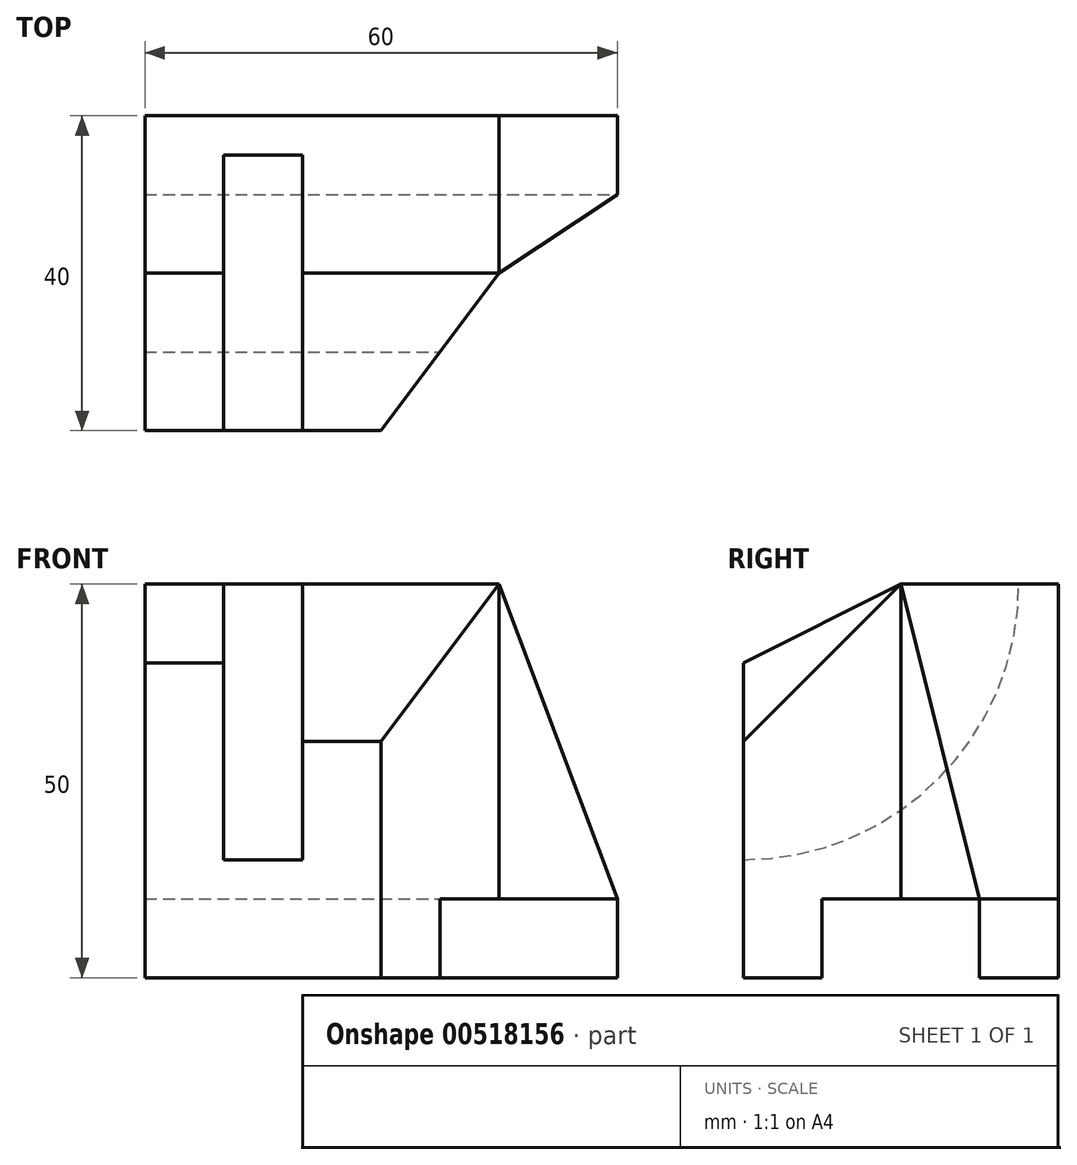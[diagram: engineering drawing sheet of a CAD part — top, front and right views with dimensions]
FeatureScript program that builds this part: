
annotation { "Feature Type Name" : "Feature", "Feature Type Description" : "" }
export const myFeature = defineFeature(function(context is Context, id is Id, definition is map)
    precondition{}
    {
        {
            var Q0;
            Q0=qCreatedBy(makeId("Front.planeOp"),FACE);
            var sketch = newSketch(context, id + "F0", { "sketchPlane" : qUnion([Q0])});
            skLineSegment(sketch, "E0.bottom", {"start": v(0, 0) * mm, "end": v(60, 0) * mm});
            skLineSegment(sketch, "E0.top", {"start": v(0, 50) * mm, "end": v(60, 50) * mm});
            skLineSegment(sketch, "E0.left", {"start": v(0, 0) * mm, "end": v(0, 50) * mm});
            skLineSegment(sketch, "E0.right", {"start": v(60, 0) * mm, "end": v(60, 50) * mm});
            skSolve(sketch);
        }
        {
            var Q0;
            Q0 = qSketchRegion(id + "F0", true);
            extrude(context, id + "F1", {"entities" : qUnion([Q0]), "depth" : 40 * mm, "offsetDistance" : 25 * mm});
        }
        {
            var Q0;
            Q0=makeQuery(id+"F1.opExtrude","CAP_FACE",FACE,{"disambiguationData":[OSD([sQuery(id+"F0.wireOp",EDGE,"E0.bottom"),sQuery(id+"F0.wireOp",EDGE,"E0.top"),sQuery(id+"F0.wireOp",EDGE,"E0.left"),sQuery(id+"F0.wireOp",EDGE,"E0.right")])],"isStart":false});
            var sketch = newSketch(context, id + "F2", { "sketchPlane" : qUnion([Q0])});
            skLineSegment(sketch, "E1.bottom", {"start": v(10, 50) * mm, "end": v(20, 50) * mm});
            skLineSegment(sketch, "E1.top", {"start": v(10, 15) * mm, "end": v(20, 15) * mm});
            skLineSegment(sketch, "E1.left", {"start": v(10, 50) * mm, "end": v(10, 15) * mm});
            skLineSegment(sketch, "E1.right", {"start": v(20, 50) * mm, "end": v(20, 15) * mm});
            skSolve(sketch);
        }
        {
            var Q0;
            Q0=makeQuery(id+"F1.opExtrude","SWEPT_FACE",FACE,{"disambiguationData":[OSD([sQuery(id+"F0.wireOp",EDGE,"E0.top")])]});
            var sketch = newSketch(context, id + "F3", { "sketchPlane" : qUnion([Q0])});
            skLineSegment(sketch, "E2.bottom", {"start": v(10, -40) * mm, "end": v(20, -40) * mm});
            skLineSegment(sketch, "E2.top", {"start": v(10, -5) * mm, "end": v(20, -5) * mm});
            skLineSegment(sketch, "E2.left", {"start": v(10, -40) * mm, "end": v(10, -5) * mm});
            skLineSegment(sketch, "E2.right", {"start": v(20, -40) * mm, "end": v(20, -5) * mm});
            skSolve(sketch);
        }
        {
            var Q0;
            Q0=sQuery(id+"F3.wireOp",VERTEX,"E2.right.start");
            var Q1;
            Q1=sQuery(id+"F3.wireOp",VERTEX,"E2.top.end");
            var Q2;
            Q2=sQuery(id+"F2.wireOp",VERTEX,"E1.top.end");
            cPlane(context, id + "F4", {"entities" : qUnion([Q0, Q1, Q2]), "cplaneType" : CPlaneType.THREE_POINT, "offset" : 25 * mm, "width" : 150 * mm, "height" : 150 * mm});
        }
        {
            var Q0;
            Q0=qCreatedBy(id+"F4.planeOp",FACE);
            var sketch = newSketch(context, id + "F5", { "sketchPlane" : qUnion([Q0])});
            skCircle(sketch, "E3", {"center": v(-40, 50) * mm, "radius": 35 * mm});
            skSolve(sketch);
        }
        {
            var Q0;
            Q0=makeQuery(id+"F5.imprint","IMPRINT",FACE,{"disambiguationData":[TD([[makeQuery(id+"F5.imprint","IMPRINT",EDGE,{"derivedFrom":sQuery(id+"F5.wireOp",EDGE,"E3")}),1.0]])]});
            extrude(context, id + "F6", {"entities" : qUnion([Q0]), "operationType" : NewBodyOperationType.REMOVE, "oppositeDirection" : true, "depth" : 10 * mm, "offsetDistance" : 25 * mm});
        }
        {
            var Q0;
            Q0=makeQuery(id+"F1.opExtrude","SWEPT_FACE",FACE,{"disambiguationData":[OSD([sQuery(id+"F0.wireOp",EDGE,"E0.left")])]});
            var sketch = newSketch(context, id + "F7", { "sketchPlane" : qUnion([Q0])});
            skLineSegment(sketch, "E4", {"start": v(20, 50) * mm, "end": v(40, 40) * mm});
            skSolve(sketch);
        }
        {
            var Q0;
            {var subQ0=sQuery(id+"F7.wireOp",EDGE,"E4");Q0=makeQuery(id+"F7.imprint","IMPRINT",FACE,{"disambiguationData":[TD([[makeQuery(id+"F7.imprint","IMPRINT",EDGE,{"derivedFrom":subQ0}),1.0]])]});}
            extrude(context, id + "F8", {"entities" : qUnion([Q0]), "operationType" : NewBodyOperationType.REMOVE, "oppositeDirection" : true, "depth" : 10 * mm, "offsetDistance" : 25 * mm});
        }
        {
            var Q0;
            Q0=makeQuery(id+"F1.opExtrude","SWEPT_FACE",FACE,{"disambiguationData":[OSD([sQuery(id+"F0.wireOp",EDGE,"E0.right")])]});
            var sketch = newSketch(context, id + "F9", { "sketchPlane" : qUnion([Q0])});
            skLineSegment(sketch, "E5.bottom", {"start": v(-30, 0) * mm, "end": v(-10, 0) * mm});
            skLineSegment(sketch, "E5.top", {"start": v(-30, 10) * mm, "end": v(-10, 10) * mm});
            skLineSegment(sketch, "E5.left", {"start": v(-30, 0) * mm, "end": v(-30, 10) * mm});
            skLineSegment(sketch, "E5.right", {"start": v(-10, 0) * mm, "end": v(-10, 10) * mm});
            skSolve(sketch);
        }
        {
            var Q0;
            Q0 = qSketchRegion(id + "F9", true);
            extrude(context, id + "F10", {"entities" : qUnion([Q0]), "operationType" : NewBodyOperationType.REMOVE, "endBound" : BoundingType.THROUGH_ALL, "oppositeDirection" : true, "depth" : 25 * mm, "offsetDistance" : 25 * mm});
        }
        {
            var Q0;
            Q0=makeQuery(id+"F3.imprint","IMPRINT",FACE,{"disambiguationData":[TD([[makeQuery(id+"F3.imprint","IMPRINT",EDGE,{"derivedFrom":sQuery(id+"F3.wireOp",EDGE,"E2.top")}),1.0]])]});
            var sketch = newSketch(context, id + "F11", { "sketchPlane" : qUnion([Q0])});
            skLineSegment(sketch, "E6", {"start": v(30, -40) * mm, "end": v(45, -20) * mm});
            skLineSegment(sketch, "E7", {"start": v(45, -20) * mm, "end": v(60, -10) * mm});
            skSolve(sketch);
        }
        {
            var Q0;
            Q0=makeQuery(id+"F2.imprint","IMPRINT",FACE,{"disambiguationData":[TD([[makeQuery(id+"F2.imprint","IMPRINT",EDGE,{"derivedFrom":sQuery(id+"F2.wireOp",EDGE,"E1.top")}),-1.0]])]});
            var sketch = newSketch(context, id + "F12", { "sketchPlane" : qUnion([Q0])});
            skLineSegment(sketch, "E8", {"start": v(30, 50) * mm, "end": v(30, 0) * mm});
            skSolve(sketch);
        }
        {
            var Q0;
            {var subQ0=sQuery(id+"F11.wireOp",EDGE,"E6");Q0=makeQuery(id+"F11.imprint","IMPRINT",FACE,{"disambiguationData":[TD([[makeQuery(id+"F11.imprint","IMPRINT",EDGE,{"derivedFrom":subQ0}),-1.0]])]});}
            extrude(context, id + "F13", {"entities" : qUnion([Q0]), "operationType" : NewBodyOperationType.REMOVE, "endBound" : BoundingType.THROUGH_ALL, "oppositeDirection" : true, "depth" : 50 * mm, "offsetDistance" : 25 * mm});
        }
        {
            var Q0;
            {var subQ0=sQuery(id+"F0.wireOp",EDGE,"E0.right");var subQ1=sQuery(id+"F0.wireOp",EDGE,"E0.top");Q0=makeQuery(id+"F6.boolean.opBoolean","SPLIT",EDGE,{"disambiguationData":[TD([makeQuery(id+"F1.opExtrude","SWEPT_FACE",FACE,{"disambiguationData":[OSD([subQ0])]})])],"derivedFrom":makeQuery(id+"F1.opExtrude","CAP_EDGE",EDGE,{"disambiguationData":[OSD([subQ1])],"isStart":false})});}
            chamfer(context, id + "F14", {"entities" : qUnion([Q0]), "width" : 20 * mm, "tangentPropagation" : true});
        }
        {
            var Q0;
            Q0=makeQuery(id+"F3.imprint","IMPRINT",FACE,{"disambiguationData":[TD([[makeQuery(id+"F3.imprint","IMPRINT",EDGE,{"derivedFrom":sQuery(id+"F3.wireOp",EDGE,"E2.top")}),1.0]])]});
            var sketch = newSketch(context, id + "F15", { "sketchPlane" : qUnion([Q0])});
            skLineSegment(sketch, "E9", {"start": v(45, -20) * mm, "end": v(45, 0) * mm});
            skSolve(sketch);
        }
        {
            var Q0;
            Q0=makeQuery(id+"F1.opExtrude","SWEPT_FACE",FACE,{"disambiguationData":[OSD([sQuery(id+"F0.wireOp",EDGE,"E0.right")])]});
            var sketch = newSketch(context, id + "F16", { "sketchPlane" : qUnion([Q0])});
            skLineSegment(sketch, "E10", {"start": v(-10, 10) * mm, "end": v(0, 10) * mm});
            skSolve(sketch);
        }
        {
            var Q0;
            Q0=makeQuery(id+"F0.imprint","IMPRINT",FACE,{"disambiguationData":[TD([[makeQuery(id+"F0.imprint","IMPRINT",EDGE,{"derivedFrom":sQuery(id+"F0.wireOp",EDGE,"E0.bottom")}),1.0]])]});
            var sketch = newSketch(context, id + "F17", { "sketchPlane" : qUnion([Q0])});
            skLineSegment(sketch, "E11", {"start": v(45, 50) * mm, "end": v(60, 10) * mm});
            skSolve(sketch);
        }
        {
            var Q0;
            {var subQ0=sQuery(id+"F17.wireOp",EDGE,"E11");Q0=makeQuery(id+"F17.imprint","IMPRINT",FACE,{"disambiguationData":[TD([[makeQuery(id+"F17.imprint","IMPRINT",EDGE,{"derivedFrom":subQ0}),1.0]])]});}
            extrude(context, id + "F18", {"entities" : qUnion([Q0]), "operationType" : NewBodyOperationType.REMOVE, "endBound" : BoundingType.THROUGH_ALL, "depth" : 25 * mm, "offsetDistance" : 25 * mm});
        }
    });
